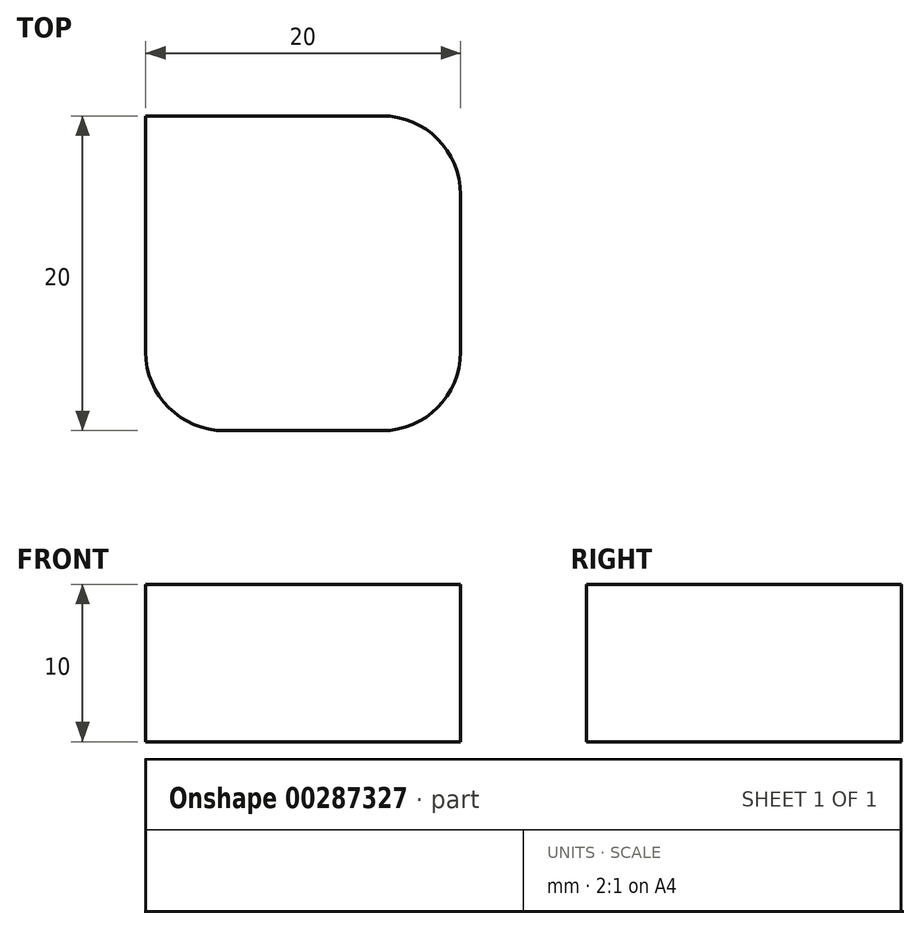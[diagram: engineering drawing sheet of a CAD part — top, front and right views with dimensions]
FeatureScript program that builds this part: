
annotation { "Feature Type Name" : "Feature", "Feature Type Description" : "" }
export const myFeature = defineFeature(function(context is Context, id is Id, definition is map)
    precondition{}
    {
        {
            var Q0;
            Q0=qCreatedBy(makeId("Top.planeOp"),FACE);
            var sketch = newSketch(context, id + "F0", { "sketchPlane" : qUnion([Q0])});
            skLineSegment(sketch, "E0.bottom", {"start": v(-10, 10) * mm, "end": v(5, 10) * mm});
            skLineSegment(sketch, "E0.top", {"start": v(-5, -10) * mm, "end": v(5, -10) * mm});
            skLineSegment(sketch, "E0.left", {"start": v(-10, 10) * mm, "end": v(-10, -5) * mm});
            skLineSegment(sketch, "E0.right", {"start": v(10, 5) * mm, "end": v(10, -5) * mm});
            skPoint(sketch, "E0.middle", {"position": v(0, 0) * mm});
            skPoint(sketch, "E1.visualSharp", {"position": v(10, 10) * mm});
            skArc(sketch, "E1.filletArc", {"start": v(10, 5) * mm, "mid": v(8.54, 8.54) * mm, "end": v(5, 10) * mm});
            skPoint(sketch, "E2.visualSharp", {"position": v(10, -10) * mm});
            skArc(sketch, "E2.filletArc", {"start": v(5, -10) * mm, "mid": v(8.54, -8.54) * mm, "end": v(10, -5) * mm});
            skPoint(sketch, "E3.visualSharp", {"position": v(-10, -10) * mm});
            skArc(sketch, "E3.filletArc", {"start": v(-10, -5) * mm, "mid": v(-8.54, -8.54) * mm, "end": v(-5, -10) * mm});
            skSolve(sketch);
        }
        {
            var Q0;
            Q0 = qSketchRegion(id + "F0", true);
            extrude(context, id + "F1", {"entities" : qUnion([Q0]), "depth" : 10 * mm});
        }
    });
